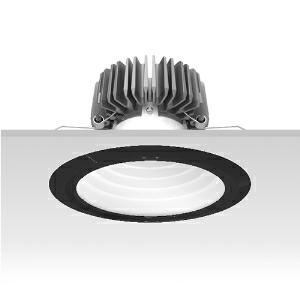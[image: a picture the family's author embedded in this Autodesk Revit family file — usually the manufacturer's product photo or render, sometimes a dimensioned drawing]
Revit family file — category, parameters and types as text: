
# Revit family: 3f_filippi_-_3f_reno_bianco_ampio_3f_filippi_-_30675_a01026_-_3f_reno_200_wh_2000-930_dali_wide___vt_bk_793a
name_source: partatom
category: Lighting Fixtures
units: mm (PartAtom-declared; Revit-internal decimal feet)

## family parameters
Cut with Voids When Loaded = No
Host = Face
Light Source = No
Part Type = Normal
Room Calculation Point = No
Round Connector Dimension = Use Diameter
Shared = No

## types (1)
- 3F Filippi - 3F Reno Bianco Ampio (1 x LED, 1804 lm, 24 W, 3000 K)
    Apparent Load = 24 VA
    Approval mark = CE
    CIE Flux Codes = 75 94 99 100 100
    Color Rendering = 90
    Color Temperature = 3000 K
    Control Gear = Electronic transformer
    Default Elevation = 1800 mm
    Description = ILLUMINOTECHNICAL
Luminous efficiency 100% (DLOR 100%, ULOR 0%).
Initial luminous flux of the luminaire 1804 lm.
Direct symmetric wide distribution.
Installation Interdistance Transv.D = 1.56 x hu - Long.D = 1.56 x hu.
Average luminance <3000 cd/m² for radial angles >65°.
Tabular UGR (CIE 117 - 4H-8H; S=0.25H; 70/50/20): RUG 20.6 - 20.5.
Beam angle: 74° - 74°.
Luminous efficacy 75 lm/W.
Lifetime (L90/B10): 30000 h. (tq+25°C)
Lifetime (L85/B10): 50000 h. (tq+25°C)
Lifetime (L70/B10): 80000 h. (tq+25°C)
Sudden decreased luminous flux after 50000 hours: 0% (C0).
Photobiological safety in compliance with IEC/TR 62778: RG0 risk exempt, (IEC 62471).
In compliance with IEC/EN 62722-2-1 - IEC/EN 62717 standards.

SOURCE
Compact LED module 2000/930.
Energy efficiency class (UE 2019/2020 - UE 2019/2015): E.
CIE 13.3 Colour rendering index: CRI >90 (R9 >50%).
IES TM-30 Fidelity Index: Rf = 92 Rg = 101.
CCT nominal colour temperature 3000 K.
Colour initial tolerance (MacAdam): SDCM 3.
Zhaga Book 3 compliant.

MECHANICAL
Passive heat dissipator in die-casting aluminium, oversized, for optimum thermal management of the LED module.
Parabolic element with graduated/concentric rings in white polycarbonate.
Transparent external lens with glossy and satin differentiated surfaces, with a cooling and anti-insect system in methacrylate (PMMA).
Fastening spring clips in stainless steel.
Dimensions: diameter 226 mm, height 146 mm. Weight 1.1 kg.
IP44 protection degree for exposed part, IP20 for recessed part.
Mechanical strength to impacts IK06 (1 joule).
Glow-wire test resistance 650°C.

ELECTRICAL
Wiring on a separate unit.
Halogen Free DALI-2 DATI (Parts 251, 252, 253), PUSH-DIM, electronic wiring 230V-50/60Hz, power factor 0.95 at full load, THD <25%, constant output current, SELV, class II, 1 driver, 1 DALI addresse.
Power of the luminaire 24 W.
ENEC - CE.
SAFE FLICKER: PstLM=<1 and SVM=<0.4 (IEC TR 61547-1 and IEC TR 63158), to ensure a more comfortable and safe light.
Luminaire compliant with EN 60598-2-22 for power supply from a centralised emergency system CPSS (Central Power Supply System), not incorporated in the luminaire - high risk areas excluded. The default power and flux are 100% in AC and 100% in DC.
Ambient temperature from 0°C to +25°C.
Temperature class T6 max 85°C.
Relative humidity UR: <85%.

INSTALLATION
Pull-up recessed fitting.
False ceiling carving: 200 mm.
All accessories dedicated to this product are available on the Catalog and on our website www.3F-Filippi.com.

ACCESSORIES
A01026 - VT transparent glass, tempered, not flammable, locked and in line with the trim, in black polycarbonate.

APPLICATIONS
Environments: architectural, commercial, exhibition areas, transit areas, corridors, shops, display windows, service areas.
In false ceilings with narrow voids.

LIGHT MANAGEMENT
Recommended minimum setting: 10%.
The luminaire, equipped with (DALI-2 DATI) driver, can be controlled manually with 3F Easy Dim technology or automatically/manually with wired or wireless DALI/D2D control systems.
The D2D driver guarantees interoperability with other devices with the same certification by making the following information available:
Device Data (Part 251), Energy Report (Part 252), Diagnosis & Maintenance (Part 253).
In electrical systems without a regulation system (manual or automatic) and DALI bus, a suitable jumper must be made on the DA-DA terminals of the appliance.

WARNING
Luminaire designed for disposal/recycling at end-of-life.
Replaceable (LED only) light source by a professional. Replaceable control gear by a professional.
    Height = 0 mm  [stored 0 ft]
    Lamp = 1 x LED
    Lamp Light Flux = 1804 lm
    Lamp Power = 24 W
    Lamp count = 1
    Length = 226 mm
    Lifetime = 50000 h
    Luminous efficacy = 75 lm/W
    Manufacturer = 3F Filippi
    ModVariant = No
    Model = 3F Filippi - 30675+A01026 - 3F Reno 200 WH 2000-930 DALI WIDE + VT BK
    Mounting Place = Ceiling
    Mounting Type = Recessed
    Number of Poles = 1
    OnlyDefault = Yes
    Power Factor = 1
    Product Name = 3F Filippi - 3F Reno Bianco Ampio
    Product group = recessed luminaire
    ProductGroupID = 4
    Protection Class = Protection class II
    Protection Degree = IP 20
    RLX_Detail_Level = 1
    RLX_Emergency_Light_Flux = 0 lm
    RLX_Emergency_Type = 0
    RLX_Emergency_Type_DB = No
    RlxData = <blob elided: 103045 chars, md5=77a79f61>
    Socket = socket
    Standby Power = 0 W
    System Light Flux = 1804 lm
    System Power = 24 W
    Type Comments = Product without accessories
    Type Image = 3ffilippi_3f_reno_200_wh__a01026.jpg
    URL = http://relux.com
    VarID = ---
    Voltage = 0 V
    Weight = 0.00 kg
    Width = 0 mm  [stored 0 ft]

note: [stored X ft] marks values corroborated as IEEE doubles in the binary element streams (Revit-internal decimal feet)

## geometry (parser evidence)
native form markers: Blend x4, Sweep x9
no freeform markers — native parametric forms only
